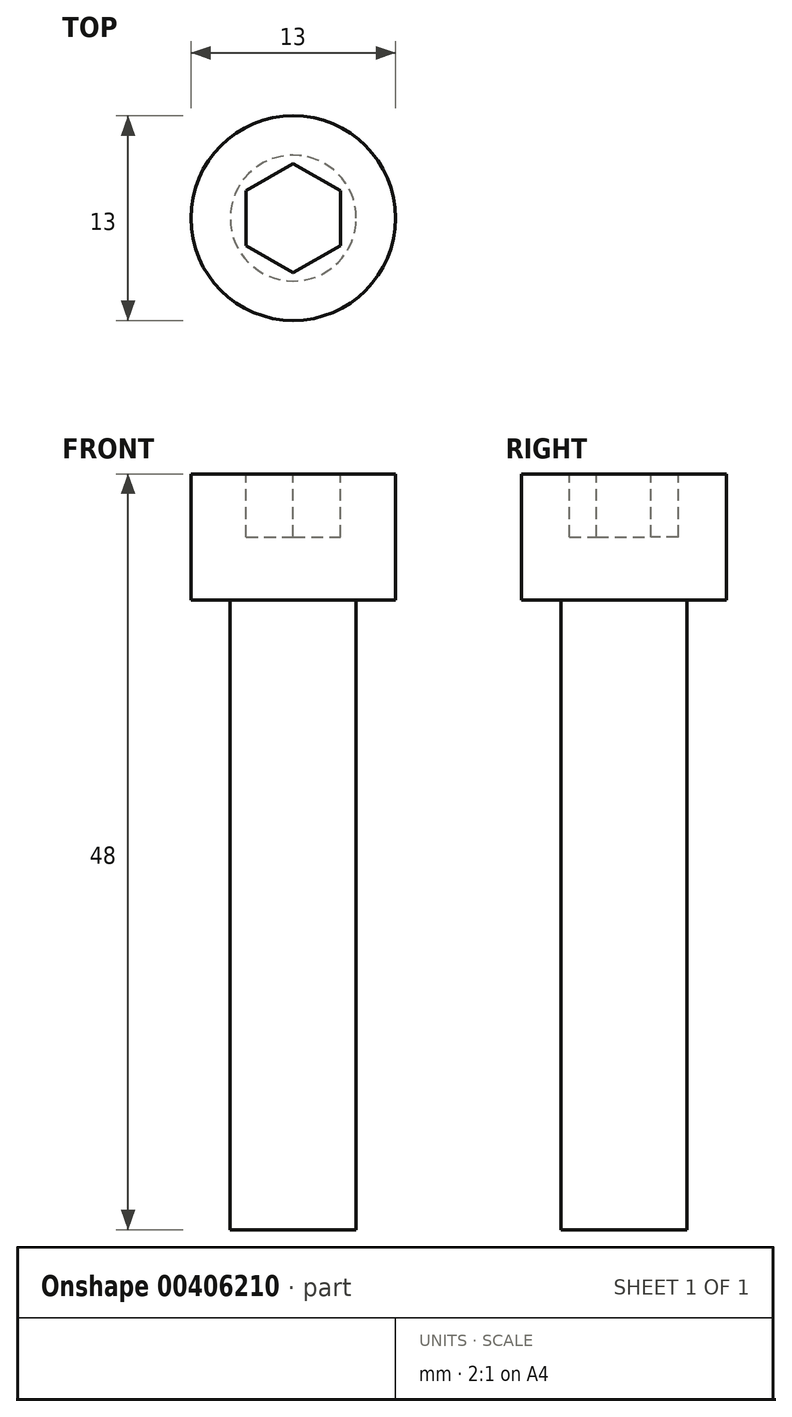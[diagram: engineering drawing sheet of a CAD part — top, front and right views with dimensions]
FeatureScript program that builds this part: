
annotation { "Feature Type Name" : "Feature", "Feature Type Description" : "" }
export const myFeature = defineFeature(function(context is Context, id is Id, definition is map)
    precondition{}
    {
        {
            var Q0;
            Q0=qCreatedBy(makeId("Top.planeOp"),FACE);
            var sketch = newSketch(context, id + "F0", { "sketchPlane" : qUnion([Q0])});
            skCircle(sketch, "E0", {"center": v(0, 0) * mm, "radius": 6.5 * mm});
            skSolve(sketch);
        }
        {
            var Q0;
            Q0 = qSketchRegion(id + "F0", true);
            extrude(context, id + "F1", {"entities" : qUnion([Q0]), "depth" : 8 * mm, "offsetDistance" : 25 * mm});
        }
        {
            var Q0;
            Q0=makeQuery(id+"F1.opExtrude","CAP_FACE",FACE,{"disambiguationData":[OSD([sQuery(id+"F0.wireOp",EDGE,"E0")])],"isStart":false});
            var sketch = newSketch(context, id + "F2", { "sketchPlane" : qUnion([Q0])});
            skCircle(sketch, "E1.cCircle", {"center": v(0, 0) * mm, "radius": 3 * mm, "construction": true});
            skLineSegment(sketch, "E1.0", {"start": v(0, 3.46) * mm, "end": v(3, 1.73) * mm});
            skLineSegment(sketch, "E1.1", {"start": v(3, 1.73) * mm, "end": v(3, -1.73) * mm});
            skLineSegment(sketch, "E1.2", {"start": v(3, -1.73) * mm, "end": v(0, -3.46) * mm});
            skLineSegment(sketch, "E1.3", {"start": v(0, -3.46) * mm, "end": v(-3, -1.73) * mm});
            skLineSegment(sketch, "E1.4", {"start": v(-3, -1.73) * mm, "end": v(-3, 1.73) * mm});
            skLineSegment(sketch, "E1.5", {"start": v(-3, 1.73) * mm, "end": v(0, 3.46) * mm});
            skPoint(sketch, "E1.0.midPoint", {"position": v(1.5, 2.6) * mm});
            skSolve(sketch);
        }
        {
            var Q0;
            Q0=makeQuery(id+"F2.imprint","IMPRINT",FACE,{"disambiguationData":[TD([[makeQuery(id+"F2.imprint","IMPRINT",EDGE,{"derivedFrom":sQuery(id+"F2.wireOp",EDGE,"E1.0")}),-1.0]])]});
            extrude(context, id + "F3", {"entities" : qUnion([Q0]), "operationType" : NewBodyOperationType.REMOVE, "oppositeDirection" : true, "depth" : 4 * mm, "offsetDistance" : 25 * mm});
        }
        {
            var Q0;
            Q0=makeQuery(id+"F1.opExtrude","CAP_FACE",FACE,{"disambiguationData":[OSD([sQuery(id+"F0.wireOp",EDGE,"E0")])],"isStart":true});
            var sketch = newSketch(context, id + "F4", { "sketchPlane" : qUnion([Q0])});
            skCircle(sketch, "E2", {"center": v(0, 0) * mm, "radius": 4 * mm});
            skSolve(sketch);
        }
        {
            var Q0;
            Q0 = qSketchRegion(id + "F4", true);
            extrude(context, id + "F5", {"entities" : qUnion([Q0]), "operationType" : NewBodyOperationType.ADD, "depth" : 40 * mm, "offsetDistance" : 25 * mm});
        }
    });
